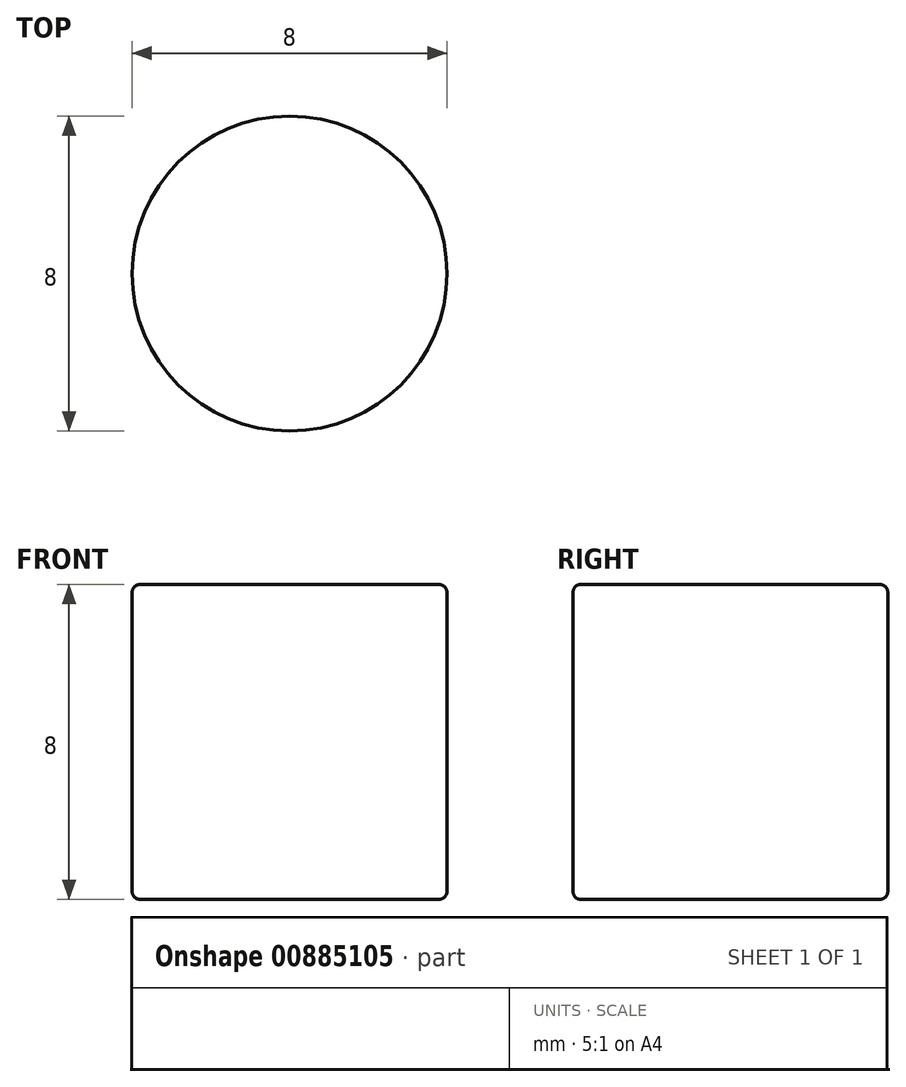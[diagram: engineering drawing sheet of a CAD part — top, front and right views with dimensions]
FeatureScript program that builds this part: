
annotation { "Feature Type Name" : "Feature", "Feature Type Description" : "" }
export const myFeature = defineFeature(function(context is Context, id is Id, definition is map)
    precondition{}
    {
        {
            var Q0;
            Q0=qCreatedBy(makeId("Top.planeOp"),FACE);
            var sketch = newSketch(context, id + "F0", { "sketchPlane" : qUnion([Q0])});
            skCircle(sketch, "E0", {"center": v(0, 0) * mm, "radius": 4 * mm});
            skSolve(sketch);
        }
        {
            var Q0;
            Q0 = qSketchRegion(id + "F0", true);
            extrude(context, id + "F1", {"entities" : qUnion([Q0]), "endBound" : BoundingType.SYMMETRIC, "depth" : 8 * mm, "offsetDistance" : 25 * mm});
        }
        {
            var Q0;
            Q0=makeQuery(id+"F1.opExtrude","CAP_FACE",FACE,{"disambiguationData":[OSD([sQuery(id+"F0.wireOp",EDGE,"E0")])],"isStart":false});
            var Q1;
            Q1=makeQuery(id+"F1.opExtrude","CAP_FACE",FACE,{"disambiguationData":[OSD([sQuery(id+"F0.wireOp",EDGE,"E0")])],"isStart":true});
            fillet(context, id + "F2", {"entities" : qUnion([Q0, Q1]), "radius" : 0.2 * mm, "tangentPropagation" : true, "allowEdgeOverflow" : false});
        }
    });
